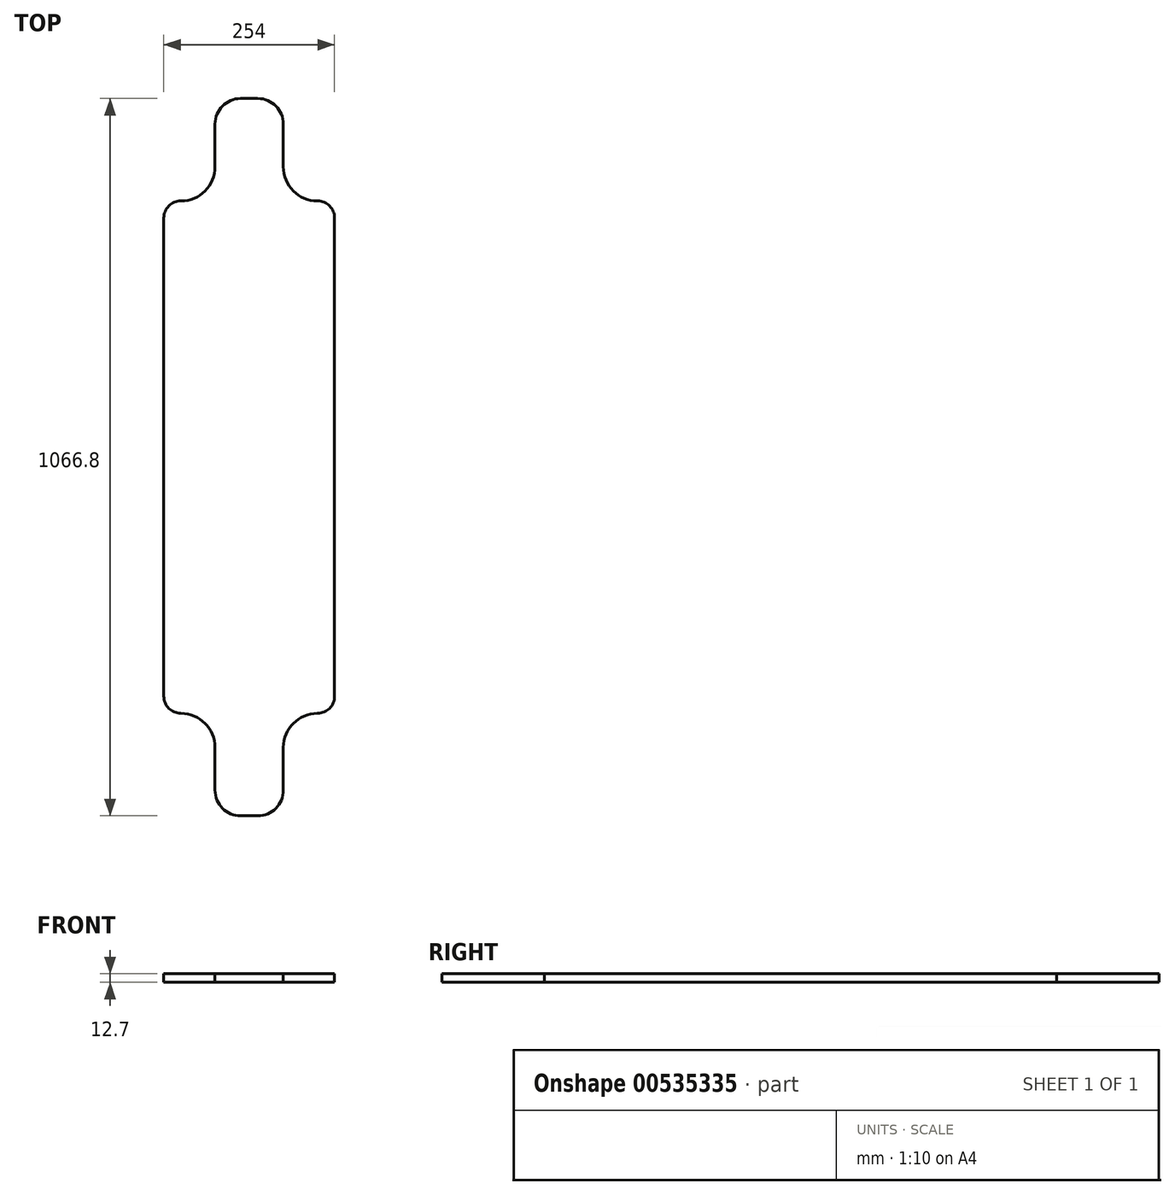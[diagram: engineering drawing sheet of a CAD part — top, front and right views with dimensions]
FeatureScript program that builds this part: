
annotation { "Feature Type Name" : "Feature", "Feature Type Description" : "" }
export const myFeature = defineFeature(function(context is Context, id is Id, definition is map)
    precondition{}
    {
        {
            var Q0;
            Q0=qCreatedBy(makeId("Top.planeOp"),FACE);
            var sketch = newSketch(context, id + "F0", { "sketchPlane" : qUnion([Q0])});
            skLineSegment(sketch, "E0.bottom", {"start": v(-127, 381) * mm, "end": v(-50.8, 381) * mm});
            skLineSegment(sketch, "E0.top", {"start": v(-127, 0) * mm, "end": v(127, 0) * mm, "construction": true});
            skLineSegment(sketch, "E0.left", {"start": v(-127, 381) * mm, "end": v(-127, 0) * mm});
            skLineSegment(sketch, "E0.right", {"start": v(127, 381) * mm, "end": v(127, 0) * mm});
            skLineSegment(sketch, "E1.top", {"start": v(-50.8, 533.4) * mm, "end": v(50.8, 533.4) * mm});
            skLineSegment(sketch, "E1.left", {"start": v(-50.8, 381) * mm, "end": v(-50.8, 533.4) * mm});
            skLineSegment(sketch, "E1.right", {"start": v(50.8, 381) * mm, "end": v(50.8, 533.4) * mm});
            skLineSegment(sketch, "E2.trimOffspring", {"start": v(50.8, 381) * mm, "end": v(127, 381) * mm});
            skLineSegment(sketch, "E3", {"start": v(0, 533.4) * mm, "end": v(0, 0) * mm, "construction": true});
            skLineSegment(sketch, "E4.MirrorCS", {"start": v(-127, -381) * mm, "end": v(-127, 0) * mm});
            skLineSegment(sketch, "E5.MirrorCS", {"start": v(-50.8, -381) * mm, "end": v(-50.8, -533.4) * mm});
            skLineSegment(sketch, "E6.MirrorCS", {"start": v(50.8, -381) * mm, "end": v(50.8, -533.4) * mm});
            skLineSegment(sketch, "E7.MirrorCS", {"start": v(-127, -381) * mm, "end": v(-50.8, -381) * mm});
            skLineSegment(sketch, "E8.MirrorCS", {"start": v(50.8, -381) * mm, "end": v(127, -381) * mm});
            skLineSegment(sketch, "E9.MirrorCS", {"start": v(-50.8, -533.4) * mm, "end": v(50.8, -533.4) * mm});
            skLineSegment(sketch, "E10.MirrorCS", {"start": v(127, -381) * mm, "end": v(127, 0) * mm});
            skSolve(sketch);
        }
        {
            var Q0;
            Q0 = qSketchRegion(id + "F0", true);
            extrude(context, id + "F1", {"entities" : qUnion([Q0]), "depth" : 12.7 * mm, "offsetDistance" : 25.4 * mm});
        }
        {
            var Q0;
            Q0=makeQuery(id+"F1.opExtrude","SWEPT_EDGE",EDGE,{"disambiguationData":[OSD([sQuery(id+"F0.wireOp",EDGE,"E0.bottom"),sQuery(id+"F0.wireOp",EDGE,"E1.left")])]});
            var Q1;
            Q1=makeQuery(id+"F1.opExtrude","SWEPT_EDGE",EDGE,{"disambiguationData":[OSD([sQuery(id+"F0.wireOp",EDGE,"E1.right"),sQuery(id+"F0.wireOp",EDGE,"E2.trimOffspring")])]});
            var Q2;
            Q2=makeQuery(id+"F1.opExtrude","SWEPT_EDGE",EDGE,{"disambiguationData":[OSD([sQuery(id+"F0.wireOp",EDGE,"E5.MirrorCS"),sQuery(id+"F0.wireOp",EDGE,"E7.MirrorCS")])]});
            var Q3;
            Q3=makeQuery(id+"F1.opExtrude","SWEPT_EDGE",EDGE,{"disambiguationData":[OSD([sQuery(id+"F0.wireOp",EDGE,"E6.MirrorCS"),sQuery(id+"F0.wireOp",EDGE,"E8.MirrorCS")])]});
            fillet(context, id + "F2", {"entities" : qUnion([Q0, Q1, Q2, Q3]), "radius" : 50.8 * mm, "tangentPropagation" : true, "allowEdgeOverflow" : false});
        }
        {
            var Q0;
            Q0=makeQuery(id+"F1.opExtrude","SWEPT_EDGE",EDGE,{"disambiguationData":[OSD([sQuery(id+"F0.wireOp",EDGE,"E1.top"),sQuery(id+"F0.wireOp",EDGE,"E1.left")])]});
            var Q1;
            Q1=makeQuery(id+"F1.opExtrude","SWEPT_EDGE",EDGE,{"disambiguationData":[OSD([sQuery(id+"F0.wireOp",EDGE,"E1.top"),sQuery(id+"F0.wireOp",EDGE,"E1.right")])]});
            var Q2;
            Q2=makeQuery(id+"F1.opExtrude","SWEPT_EDGE",EDGE,{"disambiguationData":[OSD([sQuery(id+"F0.wireOp",EDGE,"E5.MirrorCS"),sQuery(id+"F0.wireOp",EDGE,"E9.MirrorCS")])]});
            var Q3;
            Q3=makeQuery(id+"F1.opExtrude","SWEPT_EDGE",EDGE,{"disambiguationData":[OSD([sQuery(id+"F0.wireOp",EDGE,"E6.MirrorCS"),sQuery(id+"F0.wireOp",EDGE,"E9.MirrorCS")])]});
            fillet(context, id + "F3", {"entities" : qUnion([Q0, Q1, Q2, Q3]), "radius" : 38.1 * mm, "tangentPropagation" : true, "allowEdgeOverflow" : false});
        }
        {
            var Q0;
            Q0=makeQuery(id+"F1.opExtrude","SWEPT_EDGE",EDGE,{"disambiguationData":[OSD([sQuery(id+"F0.wireOp",EDGE,"E0.bottom"),sQuery(id+"F0.wireOp",EDGE,"E0.left")])]});
            var Q1;
            Q1=makeQuery(id+"F1.opExtrude","SWEPT_EDGE",EDGE,{"disambiguationData":[OSD([sQuery(id+"F0.wireOp",EDGE,"E0.right"),sQuery(id+"F0.wireOp",EDGE,"E2.trimOffspring")])]});
            var Q2;
            Q2=makeQuery(id+"F1.opExtrude","SWEPT_EDGE",EDGE,{"disambiguationData":[OSD([sQuery(id+"F0.wireOp",EDGE,"E8.MirrorCS"),sQuery(id+"F0.wireOp",EDGE,"E10.MirrorCS")])]});
            var Q3;
            Q3=makeQuery(id+"F1.opExtrude","SWEPT_EDGE",EDGE,{"disambiguationData":[OSD([sQuery(id+"F0.wireOp",EDGE,"E4.MirrorCS"),sQuery(id+"F0.wireOp",EDGE,"E7.MirrorCS")])]});
            fillet(context, id + "F4", {"entities" : qUnion([Q0, Q1, Q2, Q3]), "radius" : 25.4 * mm, "tangentPropagation" : true, "allowEdgeOverflow" : false});
        }
    });
